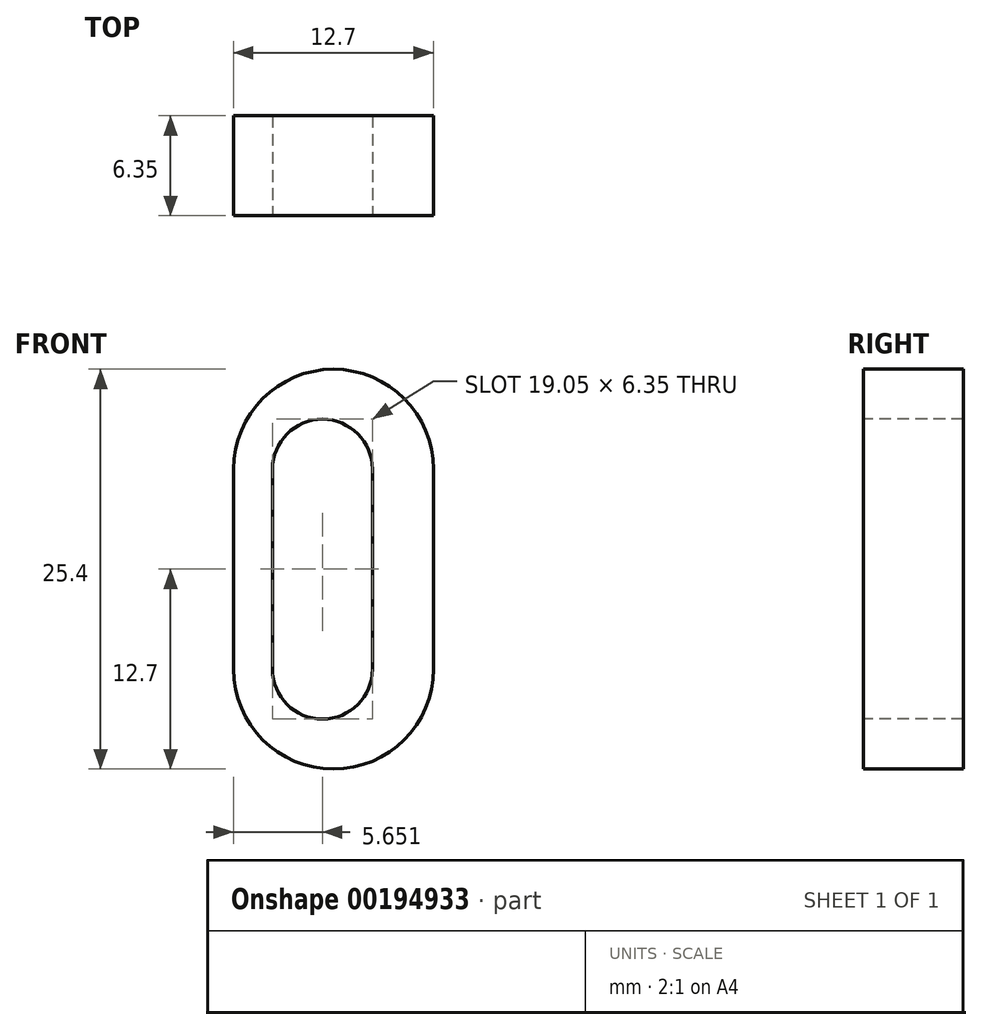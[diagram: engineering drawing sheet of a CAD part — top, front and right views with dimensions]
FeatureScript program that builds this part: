
annotation { "Feature Type Name" : "Feature", "Feature Type Description" : "" }
export const myFeature = defineFeature(function(context is Context, id is Id, definition is map)
    precondition{}
    {
        {
            var Q0;
            Q0=qCreatedBy(makeId("Front.planeOp"),FACE);
            var sketch = newSketch(context, id + "F0", { "sketchPlane" : qUnion([Q0])});
            skLineSegment(sketch, "E0.bottom", {"start": v(0, 0) * mm, "end": v(-12.7, 0) * mm});
            skLineSegment(sketch, "E0.top", {"start": v(0, 25.4) * mm, "end": v(-12.7, 25.4) * mm});
            skLineSegment(sketch, "E0.left", {"start": v(0, 0) * mm, "end": v(0, 25.4) * mm});
            skLineSegment(sketch, "E0.right", {"start": v(-12.7, 0) * mm, "end": v(-12.7, 25.4) * mm});
            skSolve(sketch);
        }
        {
            var Q0;
            Q0=makeQuery(id+"F0.imprint","IMPRINT",FACE,{"disambiguationData":[TD([[makeQuery(id+"F0.imprint","IMPRINT",EDGE,{"derivedFrom":sQuery(id+"F0.wireOp",EDGE,"E0.bottom")}),-1.0]])]});
            extrude(context, id + "F1", {"entities" : qUnion([Q0]), "depth" : 6.35 * mm});
        }
        {
            var Q0;
            Q0=makeQuery(id+"F1.opExtrude","CAP_FACE",FACE,{"disambiguationData":[OSD([sQuery(id+"F0.wireOp",EDGE,"E0.bottom"),sQuery(id+"F0.wireOp",EDGE,"E0.top"),sQuery(id+"F0.wireOp",EDGE,"E0.left"),sQuery(id+"F0.wireOp",EDGE,"E0.right")])],"isStart":false});
            var sketch = newSketch(context, id + "F2", { "sketchPlane" : qUnion([Q0])});
            skLineSegment(sketch, "E1", {"start": v(-12.7, 19.05) * mm, "end": v(-12.7, 6.35) * mm});
            skLineSegment(sketch, "E2", {"start": v(0, 6.35) * mm, "end": v(0, 19.05) * mm});
            skArc(sketch, "E3", {"start": v(-12.7, 6.35) * mm, "mid": v(-10.84, 1.86) * mm, "end": v(-6.35, 0) * mm});
            skArc(sketch, "E4", {"start": v(-6.35, 0) * mm, "mid": v(-1.86, 1.86) * mm, "end": v(0, 6.35) * mm});
            skArc(sketch, "E5", {"start": v(0, 19.05) * mm, "mid": v(-1.86, 23.54) * mm, "end": v(-6.35, 25.4) * mm});
            skArc(sketch, "E6", {"start": v(-6.35, 25.4) * mm, "mid": v(-10.84, 23.54) * mm, "end": v(-12.7, 19.05) * mm});
            skSolve(sketch);
        }
        {
            var Q0;
            {var subQ0=sQuery(id+"F2.wireOp",EDGE,"E6");Q0=makeQuery(id+"F2.imprint","IMPRINT",FACE,{"disambiguationData":[TD([[makeQuery(id+"F2.imprint","IMPRINT",EDGE,{"derivedFrom":subQ0}),-1.0]])]});}
            var Q1;
            {var subQ0=sQuery(id+"F2.wireOp",EDGE,"E5");Q1=makeQuery(id+"F2.imprint","IMPRINT",FACE,{"disambiguationData":[TD([[makeQuery(id+"F2.imprint","IMPRINT",EDGE,{"derivedFrom":subQ0}),-1.0]])]});}
            var Q2;
            {var subQ0=sQuery(id+"F2.wireOp",EDGE,"E4");Q2=makeQuery(id+"F2.imprint","IMPRINT",FACE,{"disambiguationData":[TD([[makeQuery(id+"F2.imprint","IMPRINT",EDGE,{"derivedFrom":subQ0}),-1.0]])]});}
            var Q3;
            {var subQ0=sQuery(id+"F2.wireOp",EDGE,"E3");Q3=makeQuery(id+"F2.imprint","IMPRINT",FACE,{"disambiguationData":[TD([[makeQuery(id+"F2.imprint","IMPRINT",EDGE,{"derivedFrom":subQ0}),-1.0]])]});}
            extrude(context, id + "F3", {"entities" : qUnion([Q0, Q1, Q2, Q3]), "operationType" : NewBodyOperationType.REMOVE, "oppositeDirection" : true, "depth" : 254 * mm});
        }
        {
            var Q0;
            Q0=makeQuery(id+"F1.opExtrude","CAP_FACE",FACE,{"disambiguationData":[OSD([sQuery(id+"F0.wireOp",EDGE,"E0.bottom"),sQuery(id+"F0.wireOp",EDGE,"E0.top"),sQuery(id+"F0.wireOp",EDGE,"E0.left"),sQuery(id+"F0.wireOp",EDGE,"E0.right")])],"isStart":false});
            var sketch = newSketch(context, id + "F4", { "sketchPlane" : qUnion([Q0])});
            skLineSegment(sketch, "E7.bottom", {"start": v(-2.48, 6.35) * mm, "end": v(-8.83, 6.35) * mm});
            skLineSegment(sketch, "E7.top", {"start": v(-2.48, 19.05) * mm, "end": v(-8.83, 19.05) * mm});
            skLineSegment(sketch, "E7.left", {"start": v(-2.48, 6.35) * mm, "end": v(-2.48, 19.05) * mm});
            skLineSegment(sketch, "E7.right", {"start": v(-8.83, 6.35) * mm, "end": v(-8.83, 19.05) * mm});
            skArc(sketch, "E8", {"start": v(-2.48, 19.05) * mm, "mid": v(-5.65, 22.22) * mm, "end": v(-8.83, 19.05) * mm});
            skArc(sketch, "E9", {"start": v(-8.83, 6.35) * mm, "mid": v(-5.65, 3.18) * mm, "end": v(-2.48, 6.35) * mm});
            skSolve(sketch);
        }
        {
            var Q0;
            Q0=makeQuery(id+"F4.imprint","IMPRINT",FACE,{"disambiguationData":[TD([[makeQuery(id+"F4.imprint","IMPRINT",EDGE,{"derivedFrom":sQuery(id+"F4.wireOp",EDGE,"E7.top")}),-1.0]])]});
            var Q1;
            Q1=makeQuery(id+"F4.imprint","IMPRINT",FACE,{"disambiguationData":[TD([[makeQuery(id+"F4.imprint","IMPRINT",EDGE,{"derivedFrom":sQuery(id+"F4.wireOp",EDGE,"E7.bottom")}),-1.0]])]});
            var Q2;
            Q2=makeQuery(id+"F4.imprint","IMPRINT",FACE,{"disambiguationData":[TD([[makeQuery(id+"F4.imprint","IMPRINT",EDGE,{"derivedFrom":sQuery(id+"F4.wireOp",EDGE,"E7.bottom")}),1.0]])]});
            extrude(context, id + "F5", {"entities" : qUnion([Q0, Q1, Q2]), "operationType" : NewBodyOperationType.REMOVE, "oppositeDirection" : true, "depth" : 254 * mm});
        }
        {
            var Q0;
            Q0=makeQuery(id+"F1.opExtrude","SWEPT_BODY",BODY,{"disambiguationData":[OSD([sQuery(id+"F0.wireOp",EDGE,"E0.bottom"),sQuery(id+"F0.wireOp",EDGE,"E0.top"),sQuery(id+"F0.wireOp",EDGE,"E0.left"),sQuery(id+"F0.wireOp",EDGE,"E0.right")])]});
            var Q1;
            Q1=qCreatedBy(makeId("Right.planeOp"),FACE);
            mirror(context, id + "F6", {"operationType" : NewBodyOperationType.ADD, "entities" : qUnion([Q0]), "mirrorPlane" : qUnion([Q1])});
        }
        {
            var Q0;
            {var subQ0=makeQuery(id+"F1.opExtrude","CAP_FACE",FACE,{"disambiguationData":[OSD([sQuery(id+"F0.wireOp",EDGE,"E0.bottom"),sQuery(id+"F0.wireOp",EDGE,"E0.top"),sQuery(id+"F0.wireOp",EDGE,"E0.left"),sQuery(id+"F0.wireOp",EDGE,"E0.right")])],"isStart":false});Q0=makeQuery(id+"F6.boolean.opBoolean","MERGE",FACE,{"derivedFrom":[subQ0,makeQuery(id+"F6.opPattern","COPY",FACE,{"derivedFrom":subQ0,"instanceName":"1"})]});}
            var sketch = newSketch(context, id + "F7", { "sketchPlane" : qUnion([Q0])});
            skLineSegment(sketch, "E10", {"start": v(0, 19.05) * mm, "end": v(0, 6.35) * mm});
            skSolve(sketch);
        }
        {
            var Q0;
            Q0=makeQuery(id+"F7.imprint","IMPRINT",FACE,{"disambiguationData":[TD([[makeQuery(id+"F7.imprint","IMPRINT",EDGE,{"derivedFrom":sQuery(id+"F7.wireOp",EDGE,"E10")}),-1.0]])]});
            extrude(context, id + "F8", {"entities" : qUnion([Q0]), "operationType" : NewBodyOperationType.REMOVE, "oppositeDirection" : true, "depth" : 25374.6 * mm});
        }
    });
